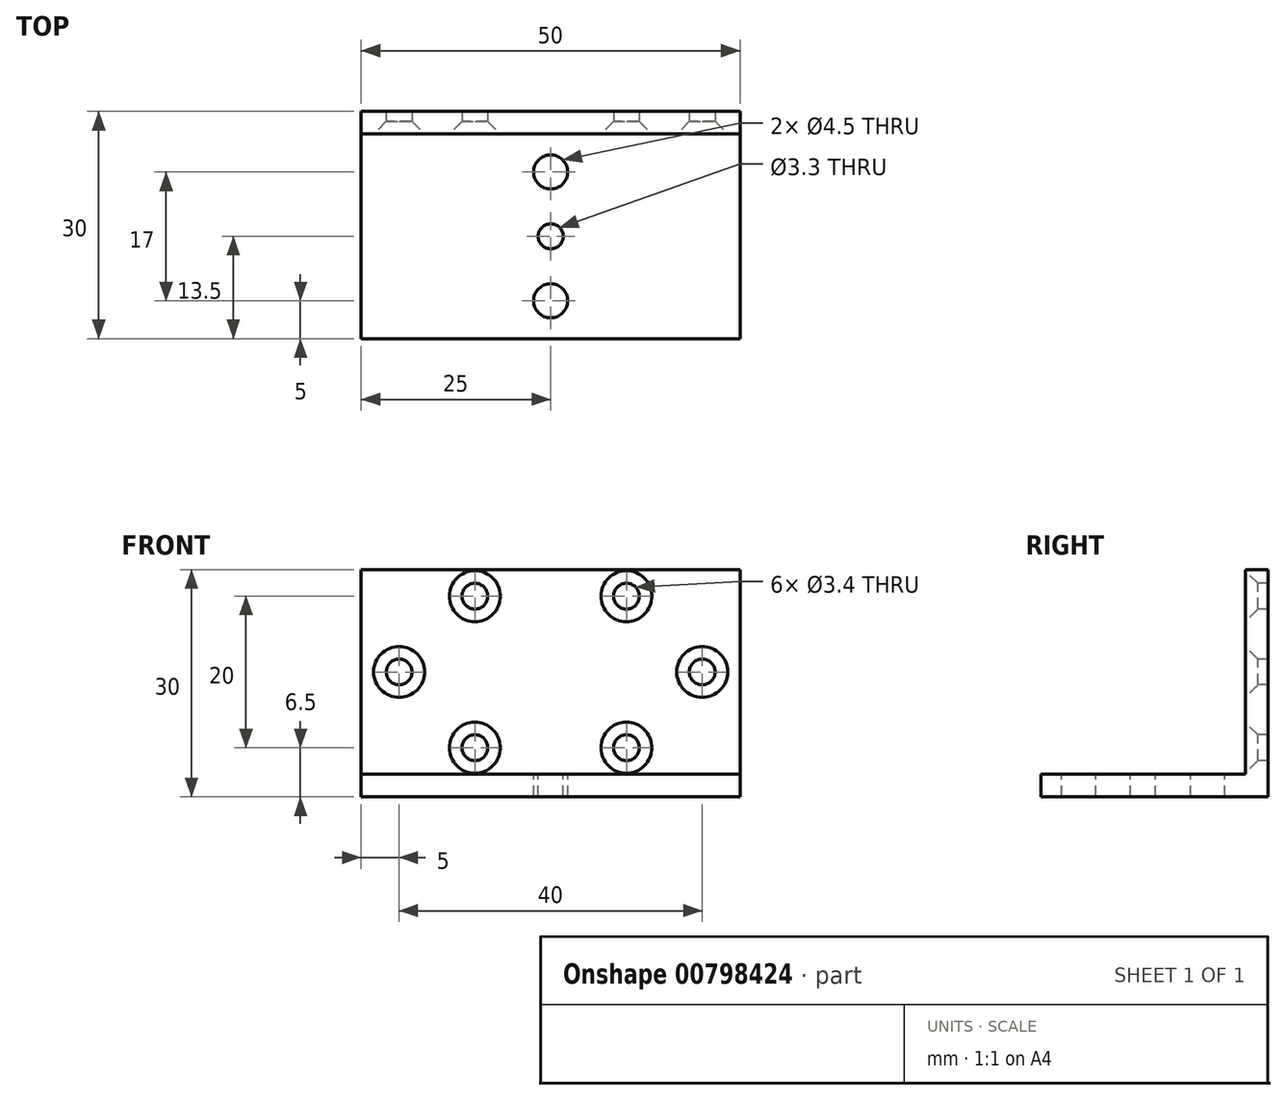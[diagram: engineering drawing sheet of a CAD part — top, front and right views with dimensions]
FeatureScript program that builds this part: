
annotation { "Feature Type Name" : "Feature", "Feature Type Description" : "" }
export const myFeature = defineFeature(function(context is Context, id is Id, definition is map)
    precondition{}
    {
        {
            var Q0;
            Q0=qCreatedBy(makeId("Front.planeOp"),FACE);
            var sketch = newSketch(context, id + "F0", { "sketchPlane" : qUnion([Q0])});
            skLineSegment(sketch, "E0.bottom", {"start": v(0, 0) * mm, "end": v(50, 0) * mm});
            skLineSegment(sketch, "E0.top", {"start": v(0, 30) * mm, "end": v(50, 30) * mm});
            skLineSegment(sketch, "E0.left", {"start": v(0, 0) * mm, "end": v(0, 30) * mm});
            skLineSegment(sketch, "E0.right", {"start": v(50, 0) * mm, "end": v(50, 30) * mm});
            skLineSegment(sketch, "E1", {"start": v(0, 3) * mm, "end": v(50, 3) * mm});
            skLineSegment(sketch, "E2", {"start": v(25, 30) * mm, "end": v(25, 3) * mm, "construction": true});
            skLineSegment(sketch, "E3", {"start": v(50, 26.5) * mm, "end": v(0, 26.5) * mm, "construction": true});
            skLineSegment(sketch, "E4", {"start": v(50, 6.5) * mm, "end": v(0, 6.5) * mm, "construction": true});
            skLineSegment(sketch, "E5", {"start": v(35, 30) * mm, "end": v(35, 3) * mm, "construction": true});
            skLineSegment(sketch, "E6", {"start": v(15, 30) * mm, "end": v(15, 3) * mm, "construction": true});
            skPoint(sketch, "E7", {"position": v(35, 26.5) * mm});
            skPoint(sketch, "E8", {"position": v(15, 26.5) * mm});
            skPoint(sketch, "E9", {"position": v(15, 6.5) * mm});
            skPoint(sketch, "E10", {"position": v(35, 6.5) * mm});
            skLineSegment(sketch, "E11", {"start": v(5, 30) * mm, "end": v(5, 3) * mm, "construction": true});
            skLineSegment(sketch, "E12", {"start": v(45, 30) * mm, "end": v(45, 3) * mm, "construction": true});
            skLineSegment(sketch, "E13", {"start": v(0, 16.5) * mm, "end": v(50, 16.5) * mm, "construction": true});
            skPoint(sketch, "E14", {"position": v(45, 16.5) * mm});
            skPoint(sketch, "E15", {"position": v(5, 16.5) * mm});
            skSolve(sketch);
        }
        {
            var Q0;
            {var subQ0=sQuery(id+"F0.wireOp",EDGE,"E0.top");Q0=makeQuery(id+"F0.imprint","IMPRINT",FACE,{"disambiguationData":[TD([[makeQuery(id+"F0.imprint","IMPRINT",EDGE,{"derivedFrom":subQ0}),-1.0]])]});}
            extrude(context, id + "F1", {"entities" : qUnion([Q0]), "oppositeDirection" : true, "depth" : 3 * mm, "offsetDistance" : 25 * mm});
        }
        {
            var Q0;
            Q0=sQuery(id+"F0.wireOp",VERTEX,"E7");
            var Q1;
            Q1=sQuery(id+"F0.wireOp",VERTEX,"E8");
            var Q2;
            Q2=sQuery(id+"F0.wireOp",VERTEX,"E9");
            var Q3;
            Q3=sQuery(id+"F0.wireOp",VERTEX,"E10");
            var Q4;
            Q4=sQuery(id+"F0.wireOp",VERTEX,"E15");
            var Q5;
            Q5=sQuery(id+"F0.wireOp",VERTEX,"E14");
            var Q6;
            Q6=makeQuery(id+"F1.opExtrude","SWEPT_BODY",BODY,{"disambiguationData":[OSD([sQuery(id+"F0.wireOp",EDGE,"E0.top"),sQuery(id+"F0.wireOp",EDGE,"E0.left"),sQuery(id+"F0.wireOp",EDGE,"E0.right"),sQuery(id+"F0.wireOp",EDGE,"E1")])]});
            hole(context, id + "F2", {"style" : HoleStyle.C_SINK, "endStyle" : HoleEndStyle.THROUGH, "standardTappedOrClearance" : lookupTablePath({ "fit" : "Normal", "standard" : "ISO", "size" : "M3", "type" : "Clearance" }), "standardBlindInLast" : lookupTablePath({ "fit" : "Normal", "standard" : "ISO", "size" : "M3", "type" : "Clearance" }), "holeDiameter" : 3.4 * mm, "cSinkDiameter" : 6.72 * mm, "cSinkAngle" : 90 * degree, "majorDiameter" : 5 * mm, "tappedDepth" : 12 * mm, "tapClearance" : 3, "locations" : qUnion([Q0, Q1, Q2, Q3, Q4, Q5]), "scope" : qUnion([Q6])});
        }
        {
            var Q0;
            Q0=makeQuery(id+"F1.opExtrude","SWEPT_FACE",FACE,{"disambiguationData":[OSD([sQuery(id+"F0.wireOp",EDGE,"E1")])]});
            extrude(context, id + "F3", {"entities" : qUnion([Q0]), "operationType" : NewBodyOperationType.ADD, "depth" : 3 * mm, "offsetDistance" : 25 * mm});
        }
        {
            var Q0;
            {var subQ0=sQuery(id+"F0.wireOp",EDGE,"E0.bottom");Q0=makeQuery(id+"F0.imprint","IMPRINT",FACE,{"disambiguationData":[TD([[makeQuery(id+"F0.imprint","IMPRINT",EDGE,{"derivedFrom":subQ0}),1.0]])]});}
            extrude(context, id + "F4", {"entities" : qUnion([Q0]), "operationType" : NewBodyOperationType.ADD, "depth" : 27 * mm, "offsetDistance" : 25 * mm});
        }
        {
            var Q0;
            Q0=makeQuery(id+"F4.opExtrude","SWEPT_FACE",FACE,{"disambiguationData":[OSD([sQuery(id+"F0.wireOp",EDGE,"E1")])]});
            var sketch = newSketch(context, id + "F5", { "sketchPlane" : qUnion([Q0])});
            skLineSegment(sketch, "E16", {"start": v(25, -27) * mm, "end": v(25, 0) * mm, "construction": true});
            skLineSegment(sketch, "E17", {"start": v(0, -22) * mm, "end": v(50, -22) * mm, "construction": true});
            skLineSegment(sketch, "E18", {"start": v(0, -5) * mm, "end": v(50, -5) * mm, "construction": true});
            skPoint(sketch, "E19", {"position": v(25, -5) * mm});
            skPoint(sketch, "E20", {"position": v(25, -22) * mm});
            skLineSegment(sketch, "E21", {"start": v(0, -13.5) * mm, "end": v(50, -13.5) * mm, "construction": true});
            skPoint(sketch, "E22", {"position": v(25, -13.5) * mm});
            skLineSegment(sketch, "E23", {"start": v(33, -27) * mm, "end": v(33, 0) * mm, "construction": true});
            skLineSegment(sketch, "E24", {"start": v(50, -2.4) * mm, "end": v(0, -2.4) * mm, "construction": true});
            skPoint(sketch, "E25", {"position": v(33, -2.4) * mm});
            skSolve(sketch);
        }
        {
            var Q0;
            Q0=sQuery(id+"F5.wireOp",VERTEX,"E22");
            var Q1;
            Q1=makeQuery(id+"F1.opExtrude","SWEPT_BODY",BODY,{"disambiguationData":[OSD([sQuery(id+"F0.wireOp",EDGE,"E0.top"),sQuery(id+"F0.wireOp",EDGE,"E0.left"),sQuery(id+"F0.wireOp",EDGE,"E0.right"),sQuery(id+"F0.wireOp",EDGE,"E1")])]});
            hole(context, id + "F6", {"style" : HoleStyle.SIMPLE, "endStyle" : HoleEndStyle.THROUGH, "standardTappedOrClearance" : lookupTablePath({ "standard" : "ISO", "engagement" : "75%", "pitch" : "0.7 mm", "size" : "M4", "type" : "Tapped" }), "standardBlindInLast" : lookupTablePath({ "standard" : "ISO", "fit" : "Normal", "engagement" : "75%", "pitch" : "0.7 mm", "size" : "M4", "type" : "Clearance & tapped" }), "holeDiameter" : 3.3 * mm, "majorDiameter" : 4 * mm, "showTappedDepth" : true, "tappedDepth" : 12 * mm, "tapClearance" : 3, "locations" : qUnion([Q0]), "scope" : qUnion([Q1])});
        }
        {
            var Q0;
            Q0=sQuery(id+"F5.wireOp",VERTEX,"E19");
            var Q1;
            Q1=sQuery(id+"F5.wireOp",VERTEX,"E20");
            var Q2;
            Q2=makeQuery(id+"F1.opExtrude","SWEPT_BODY",BODY,{"disambiguationData":[OSD([sQuery(id+"F0.wireOp",EDGE,"E0.top"),sQuery(id+"F0.wireOp",EDGE,"E0.left"),sQuery(id+"F0.wireOp",EDGE,"E0.right"),sQuery(id+"F0.wireOp",EDGE,"E1")])]});
            hole(context, id + "F7", {"style" : HoleStyle.SIMPLE, "endStyle" : HoleEndStyle.THROUGH, "standardTappedOrClearance" : lookupTablePath({ "fit" : "Normal", "standard" : "ISO", "size" : "M4", "type" : "Clearance" }), "standardBlindInLast" : lookupTablePath({ "fit" : "Normal", "standard" : "ISO", "engagement" : "75%", "pitch" : "0.7 mm", "size" : "M4", "type" : "Clearance & tapped" }), "holeDiameter" : 4.5 * mm, "majorDiameter" : 4 * mm, "tappedDepth" : 12 * mm, "tapClearance" : 3, "locations" : qUnion([Q0, Q1]), "scope" : qUnion([Q2])});
        }
    });
